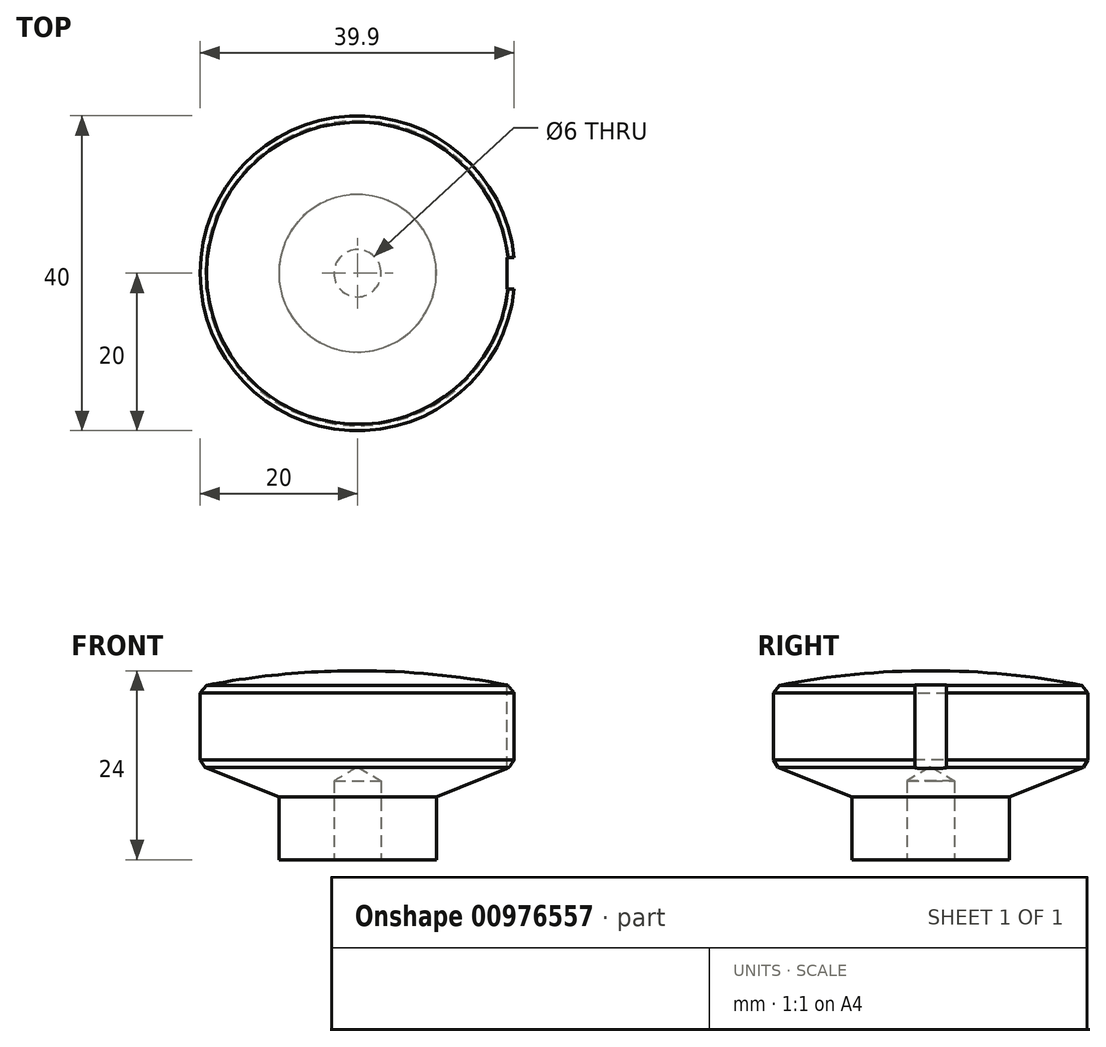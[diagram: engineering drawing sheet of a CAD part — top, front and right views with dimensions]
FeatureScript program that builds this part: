
annotation { "Feature Type Name" : "Feature", "Feature Type Description" : "" }
export const myFeature = defineFeature(function(context is Context, id is Id, definition is map)
    precondition{}
    {
        {
            var Q0;
            Q0=qCreatedBy(makeId("Front.planeOp"),FACE);
            var sketch = newSketch(context, id + "F0", { "sketchPlane" : qUnion([Q0])});
            skLineSegment(sketch, "E0", {"start": v(-20, -2) * mm, "end": v(-20, -12) * mm});
            skLineSegment(sketch, "E1", {"start": v(-20, -12) * mm, "end": v(-10, -16) * mm});
            skLineSegment(sketch, "E2", {"start": v(-10, -16) * mm, "end": v(-10, -24) * mm});
            skLineSegment(sketch, "E3", {"start": v(-10, -24) * mm, "end": v(0, -24) * mm});
            skLineSegment(sketch, "E4", {"start": v(0, -24) * mm, "end": v(0, 0) * mm});
            skLineSegment(sketch, "E5", {"start": v(0, 0) * mm, "end": v(-20, 0) * mm, "construction": true});
            skArc(sketch, "E6", {"start": v(0, 0) * mm, "mid": v(-10.05, -0.5) * mm, "end": v(-20, -2) * mm});
            skLineSegment(sketch, "E7", {"start": v(-20, -2) * mm, "end": v(-20, 0) * mm, "construction": true});
            skSolve(sketch);
        }
        {
            var Q0;
            Q0=makeQuery(id+"F0.imprint","IMPRINT",FACE,{"disambiguationData":[TD([[makeQuery(id+"F0.imprint","IMPRINT",EDGE,{"derivedFrom":sQuery(id+"F0.wireOp",EDGE,"E0")}),1.0]])]});
            var Q1;
            Q1=sQuery(id+"F0.wireOp",EDGE,"E4");
            revolve(context, id + "F1", {"surfaceOperationType" : NewSurfaceOperationType.NEW, "entities" : qUnion([Q0]), "axis" : qUnion([Q1]), "revolveType" : RevolveType.FULL});
        }
        {
            var Q0;
            Q0=makeQuery(id+"F1.opRevolve","SWEPT_EDGE",EDGE,{"disambiguationData":[OSD([sQuery(id+"F0.wireOp",EDGE,"E0"),sQuery(id+"F0.wireOp",EDGE,"E5")])]});
            var Q1;
            Q1=makeQuery(id+"F1.opRevolve","SWEPT_EDGE",EDGE,{"disambiguationData":[OSD([sQuery(id+"F0.wireOp",EDGE,"E0"),sQuery(id+"F0.wireOp",EDGE,"E1")])]});
            chamfer(context, id + "F2", {"entities" : qUnion([Q0, Q1]), "width" : 1 * mm, "tangentPropagation" : true});
        }
        {
            var Q0;
            Q0=makeQuery(id+"F1.opRevolve","SWEPT_FACE",FACE,{"disambiguationData":[OSD([sQuery(id+"F0.wireOp",EDGE,"E3")])]});
            var sketch = newSketch(context, id + "F3", { "sketchPlane" : qUnion([Q0])});
            skPoint(sketch, "E8", {"position": v(0, 0) * mm});
            skSolve(sketch);
        }
        {
            var Q0;
            Q0=sQuery(id+"F3.wireOp",VERTEX,"E8");
            var Q1;
            Q1=makeQuery(id+"F1.opRevolve","SWEPT_BODY",BODY,{"disambiguationData":[OSD([sQuery(id+"F0.wireOp",EDGE,"E0"),sQuery(id+"F0.wireOp",EDGE,"E1"),sQuery(id+"F0.wireOp",EDGE,"E2"),sQuery(id+"F0.wireOp",EDGE,"E3"),sQuery(id+"F0.wireOp",EDGE,"E4"),sQuery(id+"F0.wireOp",EDGE,"E5")])]});
            hole(context, id + "F4", {"style" : HoleStyle.SIMPLE, "endStyle" : HoleEndStyle.BLIND, "holeDiameter" : 6 * mm, "majorDiameter" : 5 * mm, "holeDepth" : 10 * mm, "isTappedThrough" : true, "tappedDepth" : 12 * mm, "tapClearance" : 3, "locations" : qUnion([Q0]), "scope" : qUnion([Q1])});
        }
        {
            var Q0;
            Q0=qCreatedBy(makeId("Top.planeOp"),FACE);
            var sketch = newSketch(context, id + "F5", { "sketchPlane" : qUnion([Q0])});
            skLineSegment(sketch, "E9.bottom", {"start": v(19, 2) * mm, "end": v(20, 2) * mm});
            skLineSegment(sketch, "E9.top", {"start": v(19, -2) * mm, "end": v(20, -2) * mm});
            skLineSegment(sketch, "E9.left", {"start": v(19, 2) * mm, "end": v(19, -2) * mm});
            skLineSegment(sketch, "E9.right", {"start": v(20, 2) * mm, "end": v(20, -2) * mm});
            skLineSegment(sketch, "E10", {"start": v(0, 0) * mm, "end": v(19, 0) * mm, "construction": true});
            skSolve(sketch);
        }
        {
            var Q0;
            Q0=makeQuery(id+"F5.imprint","IMPRINT",FACE,{"disambiguationData":[TD([[makeQuery(id+"F5.imprint","IMPRINT",EDGE,{"derivedFrom":sQuery(id+"F5.wireOp",EDGE,"E9.bottom")}),-1.0]])]});
            extrude(context, id + "F6", {"entities" : qUnion([Q0]), "operationType" : NewBodyOperationType.REMOVE, "endBound" : BoundingType.THROUGH_ALL, "oppositeDirection" : true, "depth" : 25 * mm, "offsetDistance" : 25 * mm});
        }
    });
